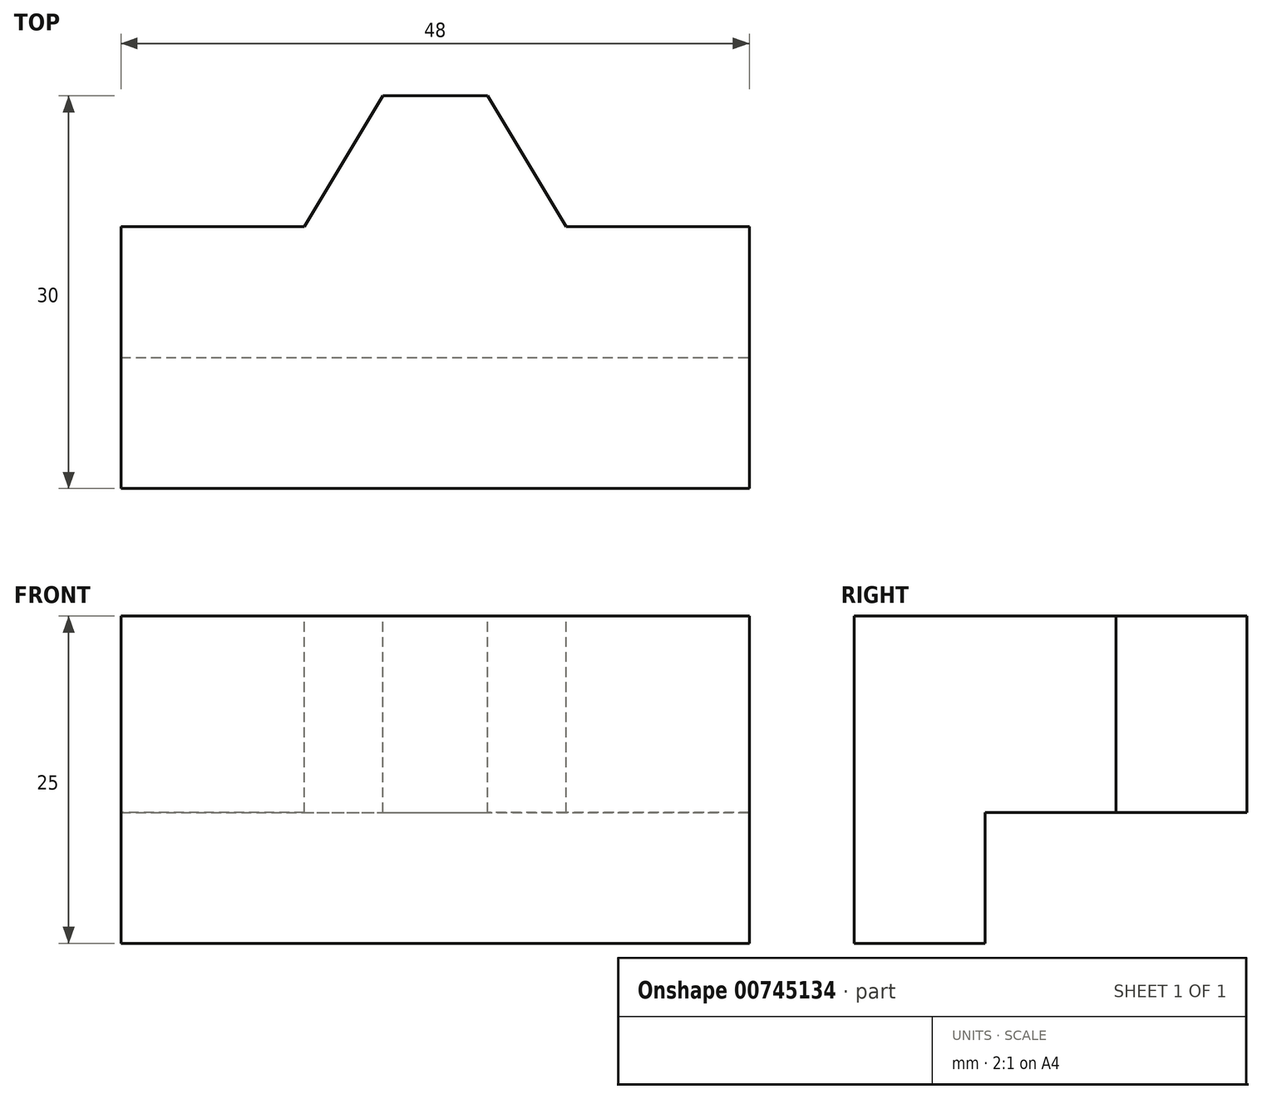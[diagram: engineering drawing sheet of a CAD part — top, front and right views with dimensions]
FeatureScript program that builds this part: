
annotation { "Feature Type Name" : "Feature", "Feature Type Description" : "" }
export const myFeature = defineFeature(function(context is Context, id is Id, definition is map)
    precondition{}
    {
        {
            var Q0;
            Q0=qCreatedBy(makeId("Front.planeOp"),FACE);
            var sketch = newSketch(context, id + "F0", { "sketchPlane" : qUnion([Q0])});
            skLineSegment(sketch, "E0.bottom", {"start": v(24, 12.5) * mm, "end": v(-24, 12.5) * mm});
            skLineSegment(sketch, "E0.top", {"start": v(24, -12.5) * mm, "end": v(-24, -12.5) * mm});
            skLineSegment(sketch, "E0.left", {"start": v(24, 12.5) * mm, "end": v(24, -12.5) * mm});
            skLineSegment(sketch, "E0.right", {"start": v(-24, 12.5) * mm, "end": v(-24, -12.5) * mm});
            skPoint(sketch, "E0.middle", {"position": v(0, 0) * mm});
            skSolve(sketch);
        }
        {
            var Q0;
            Q0=qSketchRegion(id+"F0",true);
            extrude(context, id + "F1", {"entities" : qUnion([Q0]), "oppositeDirection" : true, "depth" : 10 * mm, "offsetDistance" : 25 * mm});
        }
        {
            var Q0;
            Q0=makeQuery(id+"F1.opExtrude","SWEPT_FACE",FACE,{"disambiguationData":[OSD([sQuery(id+"F0.wireOp",EDGE,"E0.bottom")])]});
            var sketch = newSketch(context, id + "F2", { "sketchPlane" : qUnion([Q0])});
            skLineSegment(sketch, "E1", {"start": v(0, 0) * mm, "end": v(10, 0) * mm});
            skLineSegment(sketch, "E2", {"start": v(10, 0) * mm, "end": v(4, 10) * mm});
            skLineSegment(sketch, "E3", {"start": v(4, 10) * mm, "end": v(0, 10) * mm});
            skLineSegment(sketch, "E4.MirrorCS", {"start": v(-4, 10) * mm, "end": v(0, 10) * mm});
            skLineSegment(sketch, "E5.MirrorCS", {"start": v(-10, 0) * mm, "end": v(-4, 10) * mm});
            skLineSegment(sketch, "E6.MirrorCS", {"start": v(0, 0) * mm, "end": v(-10, 0) * mm});
            skSolve(sketch);
        }
        {
            var Q0;
            {var subQ0=sQuery(id+"F2.wireOp",EDGE,"E5.MirrorCS");Q0=makeQuery(id+"F2.imprint","IMPRINT",FACE,{"disambiguationData":[TD([[makeQuery(id+"F2.imprint","IMPRINT",EDGE,{"derivedFrom":subQ0}),1.0]])]});}
            var Q1;
            {var subQ0=sQuery(id+"F2.wireOp",EDGE,"E2");Q1=makeQuery(id+"F2.imprint","IMPRINT",FACE,{"disambiguationData":[TD([[makeQuery(id+"F2.imprint","IMPRINT",EDGE,{"derivedFrom":subQ0}),-1.0]])]});}
            extrude(context, id + "F3", {"entities" : qUnion([Q0, Q1]), "operationType" : NewBodyOperationType.REMOVE, "oppositeDirection" : true, "depth" : 15 * mm, "offsetDistance" : 25 * mm});
        }
        {
            var Q0;
            Q0 = qSketchRegion(id + "F0", true);
            extrude(context, id + "F4", {"entities" : qUnion([Q0]), "operationType" : NewBodyOperationType.ADD, "depth" : 20 * mm, "offsetDistance" : 25 * mm});
        }
        {
            var Q0;
            {var subQ0=sQuery(id+"F0.wireOp",EDGE,"E0.left");Q0=makeQuery(id+"F4.boolean.opBoolean","MERGE",FACE,{"derivedFrom":[makeQuery(id+"F1.opExtrude","SWEPT_FACE",FACE,{"disambiguationData":[OSD([subQ0])]}),makeQuery(id+"F4.opExtrude","SWEPT_FACE",FACE,{"disambiguationData":[OSD([subQ0])]})]});}
            var sketch = newSketch(context, id + "F5", { "sketchPlane" : qUnion([Q0])});
            skLineSegment(sketch, "E7.bottom", {"start": v(10, -12.5) * mm, "end": v(-10, -12.5) * mm});
            skLineSegment(sketch, "E7.top", {"start": v(10, -2.5) * mm, "end": v(-10, -2.5) * mm});
            skLineSegment(sketch, "E7.left", {"start": v(10, -12.5) * mm, "end": v(10, -2.5) * mm});
            skLineSegment(sketch, "E7.right", {"start": v(-10, -12.5) * mm, "end": v(-10, -2.5) * mm});
            skSolve(sketch);
        }
        {
            var Q0;
            Q0 = qSketchRegion(id + "F5", true);
            extrude(context, id + "F6", {"entities" : qUnion([Q0]), "operationType" : NewBodyOperationType.REMOVE, "oppositeDirection" : true, "depth" : 48 * mm, "offsetDistance" : 25 * mm});
        }
    });
